# Revit family: ARKOSLIGHT_Line Micro 1000 24V
name_source: partatom
category: Lighting Fixtures
units: mm (PartAtom-declared; Revit-internal decimal feet)

## family parameters
Cut with Voids When Loaded = No
Host = Face
Light Source = No
Part Type = Normal
Room Calculation Point = No
Round Connector Dimension = Use Diameter
Shared = No

## types (4) — shared parameters
ARKOSLIGHT_Apparent Load = 9 VA
ARKOSLIGHT_Beam Angle = 113.00°
ARKOSLIGHT_CRI = CRI>90
ARKOSLIGHT_Dimming = No Dim
ARKOSLIGHT_Fixture Type = TRACKLIGHTS
ARKOSLIGHT_IP = 20
ARKOSLIGHT_Model = MINIMAL TRACK
ARKOSLIGHT_Series = LINE MICRO 1000 24V
ARKOSLIGHT_Wattage = 10 W
Apparent Load = 9 VA
Description = Not valid for Minimal Track 24V Trimless
Manufacturer = ARKOSLIGHT
Model = MINIMAL TRACK
URL = https://www.arkoslight.com
zero-valued in all types: Default Elevation

## per-type parameters (varying)
| type | ARKOSLIGHT_Body Color | ARKOSLIGHT_CCT | ARKOSLIGHT_Color | ARKOSLIGHT_Efficiency | ARKOSLIGHT_IES | ARKOSLIGHT_Luminous flux | ARKOSLIGHT_Reference | IES |
| A3952000N - LINE MICRO 1000 24V 2700K N | ARKOSLIGHT_Matt black | 2700 K | Matt black | 52% | A395-20-00 N LINE MICRO 1000 24V 2700K.ies | 1430 lm | A3952000N | IES : A3952000N - LINE MICRO 1000 24V 2700K N |
| A3952001N - LINE MICRO 1000 24V 3000K N | ARKOSLIGHT_Matt black | 3000 K | Matt black | 52% | A395-20-01 N LINE MICRO 1000 24V 3000K.ies | 1500 lm | A3952001N | IES : A3952001N - LINE MICRO 1000 24V 3000K N |
| A3952000WT - LINE MICRO 1000 24V 2700K WT | ARKOSLIGHT_Textured white | 2700 K | Textured white | 70% | A395-20-00 WT LINE MICRO 1000 24V 2700K.ies | 1430 lm | A3952000WT | IES : A3952000WT - LINE MICRO 1000 24V 2700K WT |
| A3952001WT - LINE MICRO 1000 24V 3000K WT | ARKOSLIGHT_Textured white | 3000 K | Textured white | 70% | A395-20-01 WT LINE MICRO 1000 24V 3000K.ies | 1500 lm | A3952001WT | IES : A3952001WT - LINE MICRO 1000 24V 3000K WT |

## geometry (parser evidence)
native form markers: Sweep x5
no freeform markers — native parametric forms only
